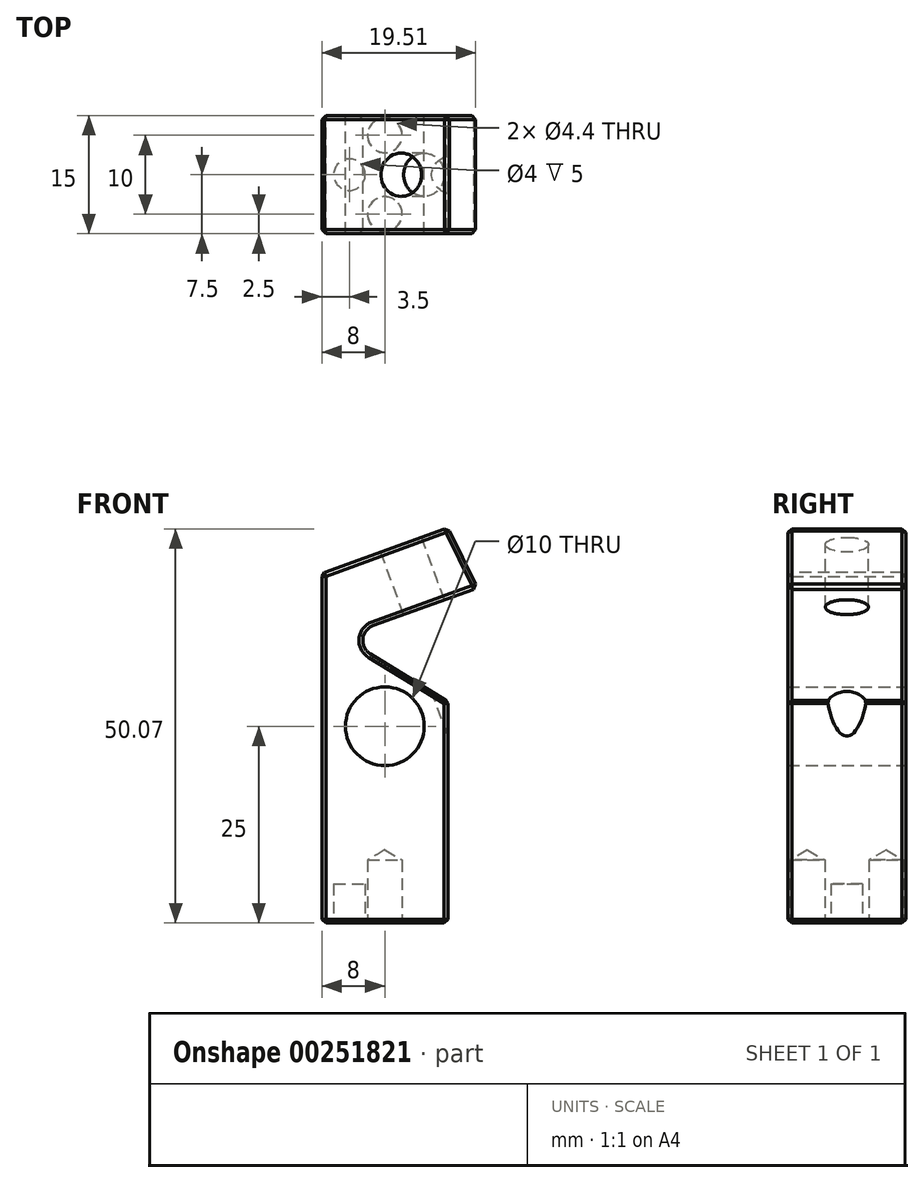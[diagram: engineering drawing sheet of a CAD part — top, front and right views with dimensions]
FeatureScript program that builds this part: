
annotation { "Feature Type Name" : "Feature", "Feature Type Description" : "" }
export const myFeature = defineFeature(function(context is Context, id is Id, definition is map)
    precondition{}
    {
        {
            var Q0;
            Q0=qCreatedBy(makeId("Front.planeOp"),FACE);
            var sketch = newSketch(context, id + "F0", { "sketchPlane" : qUnion([Q0])});
            skCircle(sketch, "E0", {"center": v(0, 0) * mm, "radius": 5 * mm});
            skLineSegment(sketch, "E1", {"start": v(-8, 19.4) * mm, "end": v(-8, -25) * mm});
            skLineSegment(sketch, "E2", {"start": v(-8, -25) * mm, "end": v(8, -25) * mm});
            skLineSegment(sketch, "E3", {"start": v(8, -25) * mm, "end": v(8, 3.16) * mm});
            skLineSegment(sketch, "E4", {"start": v(-20.9, 10.9) * mm, "end": v(20.47, 10.9) * mm, "construction": true});
            skLineSegment(sketch, "E5", {"start": v(-0.8, 16.83) * mm, "end": v(-0.8, 7.43) * mm, "construction": true});
            skLineSegment(sketch, "E6", {"start": v(-8, 19.4) * mm, "end": v(8, 25.22) * mm});
            skLineSegment(sketch, "E7", {"start": v(-0.3, 25.22) * mm, "end": v(19.53, 25.22) * mm, "construction": true});
            skLineSegment(sketch, "E8", {"start": v(8, 25.22) * mm, "end": v(11.76, 17.6) * mm});
            skLineSegment(sketch, "E9", {"start": v(11.76, 17.6) * mm, "end": v(-1.48, 12.78) * mm});
            skLineSegment(sketch, "E10", {"start": v(8, 3.16) * mm, "end": v(-1.84, 9.2) * mm});
            skArc(sketch, "E11", {"start": v(-1.48, 12.78) * mm, "mid": v(-2.79, 11.1) * mm, "end": v(-1.84, 9.2) * mm});
            skSolve(sketch);
        }
        {
            var Q0;
            Q0 = qSketchRegion(id + "F0", true);
            extrude(context, id + "F1", {"entities" : qUnion([Q0]), "depth" : 15 * mm});
        }
        {
            var Q0;
            Q0=makeQuery(id+"F1.opExtrude","SWEPT_FACE",FACE,{"disambiguationData":[OSD([sQuery(id+"F0.wireOp",EDGE,"E6")])]});
            var sketch = newSketch(context, id + "F2", { "sketchPlane" : qUnion([Q0])});
            skPoint(sketch, "E12", {"position": v(9.84, -7.5) * mm});
            skSolve(sketch);
        }
        {
            var Q0;
            Q0=sQuery(id+"F2.wireOp",VERTEX,"E12");
            var Q1;
            Q1=makeQuery(id+"F1.opExtrude","SWEPT_BODY",BODY,{"disambiguationData":[OSD([sQuery(id+"F0.wireOp",EDGE,"E0"),sQuery(id+"F0.wireOp",EDGE,"E1"),sQuery(id+"F0.wireOp",EDGE,"E2"),sQuery(id+"F0.wireOp",EDGE,"E3"),sQuery(id+"F0.wireOp",EDGE,"E6"),sQuery(id+"F0.wireOp",EDGE,"E8"),sQuery(id+"F0.wireOp",EDGE,"E9"),sQuery(id+"F0.wireOp",EDGE,"E10"),sQuery(id+"F0.wireOp",EDGE,"E11")])]});
            hole(context, id + "F3", {"style" : HoleStyle.SIMPLE, "endStyle" : HoleEndStyle.THROUGH, "standardTappedOrClearance" : lookupTablePath({ "standard" : "ISO", "fit" : "Normal", "size" : "M5", "type" : "Clearance" }), "standardBlindInLast" : lookupTablePath({ "fit" : "Standard", "standard" : "ISO", "size" : "M5", "type" : "Clearance" }), "holeDiameter" : 5.5 * mm, "tappedDepth" : 12 * mm, "tapClearance" : 3, "locations" : qUnion([Q0]), "scope" : qUnion([Q1])});
        }
        {
            var Q0;
            Q0=makeQuery(id+"F1.opExtrude","SWEPT_FACE",FACE,{"disambiguationData":[OSD([sQuery(id+"F0.wireOp",EDGE,"E2")])]});
            var sketch = newSketch(context, id + "F4", { "sketchPlane" : qUnion([Q0])});
            skLineSegment(sketch, "E13", {"start": v(0, 18.58) * mm, "end": v(0, -8.08) * mm, "construction": true});
            skPoint(sketch, "E14", {"position": v(-4.5, 7.5) * mm});
            skPoint(sketch, "E15", {"position": v(0, 12.5) * mm});
            skPoint(sketch, "E16", {"position": v(0, 2.5) * mm});
            skPoint(sketch, "E17.0", {"position": v(-8, 15) * mm});
            skPoint(sketch, "E18.0", {"position": v(8, 15) * mm});
            skCircle(sketch, "E19", {"center": v(-4.5, 7.5) * mm, "radius": 2 * mm});
            skSolve(sketch);
        }
        {
            var Q0;
            Q0=sQuery(id+"F4.wireOp",VERTEX,"E15");
            var Q1;
            Q1=sQuery(id+"F4.wireOp",VERTEX,"E16");
            var Q2;
            Q2=makeQuery(id+"F1.opExtrude","SWEPT_BODY",BODY,{"disambiguationData":[OSD([sQuery(id+"F0.wireOp",EDGE,"E0"),sQuery(id+"F0.wireOp",EDGE,"E1"),sQuery(id+"F0.wireOp",EDGE,"E2"),sQuery(id+"F0.wireOp",EDGE,"E3"),sQuery(id+"F0.wireOp",EDGE,"E6"),sQuery(id+"F0.wireOp",EDGE,"E8"),sQuery(id+"F0.wireOp",EDGE,"E9"),sQuery(id+"F0.wireOp",EDGE,"E10"),sQuery(id+"F0.wireOp",EDGE,"E11")])]});
            hole(context, id + "F5", {"style" : HoleStyle.SIMPLE, "endStyle" : HoleEndStyle.BLIND, "standardTappedOrClearance" : lookupTablePath({ "standard" : "ISO", "fit" : "Normal", "size" : "M4", "type" : "Clearance" }), "standardBlindInLast" : lookupTablePath({ "fit" : "Standard", "standard" : "ISO", "size" : "M4", "type" : "Clearance" }), "holeDiameter" : 4.4 * mm, "holeDepth" : 8 * mm, "tappedDepth" : 12 * mm, "tapClearance" : 3, "locations" : qUnion([Q0, Q1]), "scope" : qUnion([Q2])});
        }
        {
            var Q0;
            Q0=makeQuery(id+"F4.imprint","IMPRINT",FACE,{"disambiguationData":[TD([[makeQuery(id+"F4.imprint","IMPRINT",EDGE,{"derivedFrom":sQuery(id+"F4.wireOp",EDGE,"E19")}),1.0]])]});
            extrude(context, id + "F6", {"entities" : qUnion([Q0]), "operationType" : NewBodyOperationType.REMOVE, "oppositeDirection" : true, "depth" : 5 * mm});
        }
        {
            var Q0;
            Q0=makeQuery(id+"F1.opExtrude","CAP_EDGE",EDGE,{"disambiguationData":[OSD([sQuery(id+"F0.wireOp",EDGE,"E3")])],"isStart":false});
            var Q1;
            Q1=makeQuery(id+"F1.opExtrude","SWEPT_EDGE",EDGE,{"disambiguationData":[OSD([sQuery(id+"F0.wireOp",EDGE,"E2"),sQuery(id+"F0.wireOp",EDGE,"E3")])]});
            var Q2;
            Q2=makeQuery(id+"F1.opExtrude","CAP_EDGE",EDGE,{"disambiguationData":[OSD([sQuery(id+"F0.wireOp",EDGE,"E2")])],"isStart":false});
            var Q3;
            Q3=makeQuery(id+"F1.opExtrude","CAP_EDGE",EDGE,{"disambiguationData":[OSD([sQuery(id+"F0.wireOp",EDGE,"E1")])],"isStart":false});
            var Q4;
            Q4=makeQuery(id+"F1.opExtrude","CAP_EDGE",EDGE,{"disambiguationData":[OSD([sQuery(id+"F0.wireOp",EDGE,"E6")])],"isStart":false});
            var Q5;
            Q5=makeQuery(id+"F1.opExtrude","CAP_EDGE",EDGE,{"disambiguationData":[OSD([sQuery(id+"F0.wireOp",EDGE,"E9")])],"isStart":false});
            var Q6;
            Q6=makeQuery(id+"F1.opExtrude","CAP_EDGE",EDGE,{"disambiguationData":[OSD([sQuery(id+"F0.wireOp",EDGE,"E8")])],"isStart":false});
            var Q7;
            Q7=makeQuery(id+"F1.opExtrude","SWEPT_EDGE",EDGE,{"disambiguationData":[OSD([sQuery(id+"F0.wireOp",EDGE,"E8"),sQuery(id+"F0.wireOp",EDGE,"E9")])]});
            var Q8;
            Q8=makeQuery(id+"F1.opExtrude","SWEPT_EDGE",EDGE,{"disambiguationData":[OSD([sQuery(id+"F0.wireOp",EDGE,"E6"),sQuery(id+"F0.wireOp",EDGE,"E8")])]});
            var Q9;
            Q9=makeQuery(id+"F1.opExtrude","CAP_EDGE",EDGE,{"disambiguationData":[OSD([sQuery(id+"F0.wireOp",EDGE,"E8")])],"isStart":true});
            var Q10;
            Q10=makeQuery(id+"F1.opExtrude","CAP_EDGE",EDGE,{"disambiguationData":[OSD([sQuery(id+"F0.wireOp",EDGE,"E9")])],"isStart":true});
            var Q11;
            Q11=makeQuery(id+"F1.opExtrude","CAP_EDGE",EDGE,{"disambiguationData":[OSD([sQuery(id+"F0.wireOp",EDGE,"E10")])],"isStart":true});
            var Q12;
            Q12=makeQuery(id+"F1.opExtrude","CAP_EDGE",EDGE,{"disambiguationData":[OSD([sQuery(id+"F0.wireOp",EDGE,"E11")])],"isStart":true});
            var Q13;
            Q13=makeQuery(id+"F1.opExtrude","CAP_EDGE",EDGE,{"disambiguationData":[OSD([sQuery(id+"F0.wireOp",EDGE,"E10")])],"isStart":false});
            var Q14;
            Q14=makeQuery(id+"F1.opExtrude","CAP_EDGE",EDGE,{"disambiguationData":[OSD([sQuery(id+"F0.wireOp",EDGE,"E11")])],"isStart":false});
            var Q15;
            {var subQ0=sQuery(id+"F0.wireOp",EDGE,"E10");var subQ1=sQuery(id+"F0.wireOp",EDGE,"E3");Q15=makeQuery(id+"F3.hole-0.boolean.opBoolean","SPLIT",EDGE,{"disambiguationData":[TD([makeQuery(id+"F1.opExtrude","CAP_FACE",FACE,{"disambiguationData":[OSD([sQuery(id+"F0.wireOp",EDGE,"E0"),sQuery(id+"F0.wireOp",EDGE,"E1"),sQuery(id+"F0.wireOp",EDGE,"E2"),subQ1,sQuery(id+"F0.wireOp",EDGE,"E6"),sQuery(id+"F0.wireOp",EDGE,"E8"),sQuery(id+"F0.wireOp",EDGE,"E9"),subQ0,sQuery(id+"F0.wireOp",EDGE,"E11")])],"isStart":false})])],"derivedFrom":makeQuery(id+"F1.opExtrude","SWEPT_EDGE",EDGE,{"disambiguationData":[OSD([subQ1,subQ0])]})});}
            var Q16;
            {var subQ0=sQuery(id+"F0.wireOp",EDGE,"E10");var subQ1=sQuery(id+"F0.wireOp",EDGE,"E3");Q16=makeQuery(id+"F3.hole-0.boolean.opBoolean","SPLIT",EDGE,{"disambiguationData":[TD([makeQuery(id+"F1.opExtrude","CAP_FACE",FACE,{"disambiguationData":[OSD([sQuery(id+"F0.wireOp",EDGE,"E0"),sQuery(id+"F0.wireOp",EDGE,"E1"),sQuery(id+"F0.wireOp",EDGE,"E2"),subQ1,sQuery(id+"F0.wireOp",EDGE,"E6"),sQuery(id+"F0.wireOp",EDGE,"E8"),sQuery(id+"F0.wireOp",EDGE,"E9"),subQ0,sQuery(id+"F0.wireOp",EDGE,"E11")])],"isStart":true})])],"derivedFrom":makeQuery(id+"F1.opExtrude","SWEPT_EDGE",EDGE,{"disambiguationData":[OSD([subQ1,subQ0])]})});}
            var Q17;
            Q17=makeQuery(id+"F1.opExtrude","CAP_EDGE",EDGE,{"disambiguationData":[OSD([sQuery(id+"F0.wireOp",EDGE,"E3")])],"isStart":true});
            var Q18;
            Q18=makeQuery(id+"F1.opExtrude","CAP_EDGE",EDGE,{"disambiguationData":[OSD([sQuery(id+"F0.wireOp",EDGE,"E2")])],"isStart":true});
            var Q19;
            Q19=makeQuery(id+"F1.opExtrude","SWEPT_EDGE",EDGE,{"disambiguationData":[OSD([sQuery(id+"F0.wireOp",EDGE,"E1"),sQuery(id+"F0.wireOp",EDGE,"E2")])]});
            var Q20;
            Q20=makeQuery(id+"F1.opExtrude","CAP_EDGE",EDGE,{"disambiguationData":[OSD([sQuery(id+"F0.wireOp",EDGE,"E1")])],"isStart":true});
            var Q21;
            Q21=makeQuery(id+"F1.opExtrude","SWEPT_EDGE",EDGE,{"disambiguationData":[OSD([sQuery(id+"F0.wireOp",EDGE,"E1"),sQuery(id+"F0.wireOp",EDGE,"E6")])]});
            var Q22;
            Q22=makeQuery(id+"F1.opExtrude","CAP_EDGE",EDGE,{"disambiguationData":[OSD([sQuery(id+"F0.wireOp",EDGE,"E6")])],"isStart":true});
            chamfer(context, id + "F7", {"entities" : qUnion([Q0, Q1, Q2, Q3, Q4, Q5, Q6, Q7, Q8, Q9, Q10, Q11, Q12, Q13, Q14, Q15, Q16, Q17, Q18, Q19, Q20, Q21, Q22]), "chamferType" : ChamferType.OFFSET_ANGLE, "width" : .5 * mm, "oppositeDirection" : false, "angle" : 45 * degree, "tangentPropagation" : true});
        }
    });
